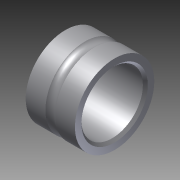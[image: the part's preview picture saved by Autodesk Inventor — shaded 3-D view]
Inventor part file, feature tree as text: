
AUTODESK INVENTOR PART (.ipt)
format: ipt  version: 2013 SP2 (Build 170200200, 200)  size: 131,072 bytes
history: native  units: mm
features: other x7, revolve x1, sketch x1
ambient origin geometry x8: Origin, YZ Plane, XZ Plane, XY Plane, X Axis, Y Axis, Z Axis, Center Point
bodies: Solid1 (feature_tree)
feature tree (9):
  revolve  "Revolution1"  [1 undecoded]
  other  "center_or_XY"
  other  "center_or_YZ"
  other  "center_or_ZX"
  other  "center_or_X"
  other  "center_or_Y"
  other  "center_or_Z"
  other  "center_or_Center"
  sketch  "Sketch_2"  dims[d0=360.0deg]
note: 1 required parameter value undecoded (feature->parameter linkage not recoverable at this tier; creation-order binding heuristic only, values carry confidence <= 0.55)
